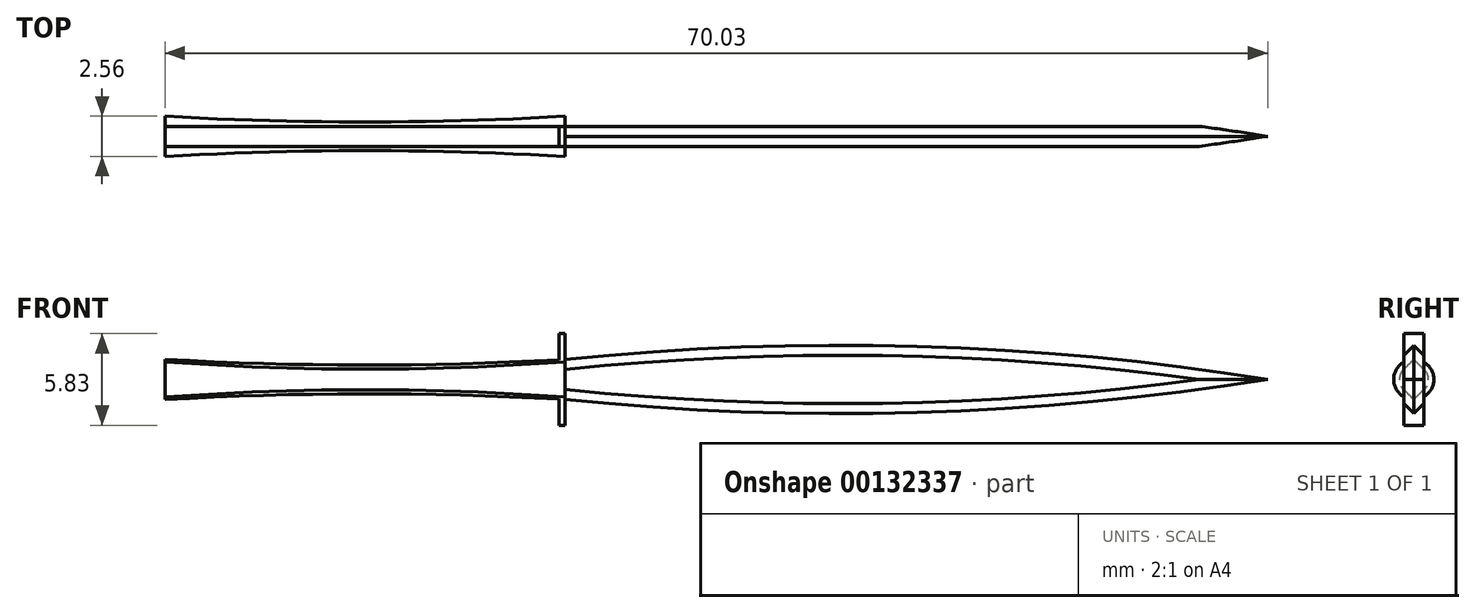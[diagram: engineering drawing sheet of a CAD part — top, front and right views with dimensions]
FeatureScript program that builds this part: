
annotation { "Feature Type Name" : "Feature", "Feature Type Description" : "" }
export const myFeature = defineFeature(function(context is Context, id is Id, definition is map)
    precondition{}
    {
        {
            var Q0;
            Q0=qCreatedBy(makeId("Front.planeOp"),FACE);
            var sketch = newSketch(context, id + "F0", { "sketchPlane" : qUnion([Q0])});
            skLineSegment(sketch, "E0", {"start": v(0, 0) * mm, "end": v(0, 2.55) * mm});
            skLineSegment(sketch, "E1", {"start": v(-25.4, 2.55) * mm, "end": v(-25.4, 0) * mm});
            skLineSegment(sketch, "E2", {"start": v(-25.4, 1.28) * mm, "end": v(0, 1.28) * mm});
            skLineSegment(sketch, "E3", {"start": v(0, 2.55) * mm, "end": v(0, 4.2) * mm});
            skLineSegment(sketch, "E4", {"start": v(0, 4.2) * mm, "end": v(-0.39, 4.2) * mm});
            skLineSegment(sketch, "E5.MirrorCS", {"start": v(0, -1.64) * mm, "end": v(-0.39, -1.64) * mm});
            skLineSegment(sketch, "E6.MirrorCS", {"start": v(0, 0) * mm, "end": v(0, -1.64) * mm});
            skLineSegment(sketch, "E7", {"start": v(0, 1.28) * mm, "end": v(44.62, 1.28) * mm});
            skArc(sketch, "E8", {"start": v(-25.4, 2.55) * mm, "mid": v(-12.7, 2.19) * mm, "end": v(0, 2.55) * mm});
            skArc(sketch, "E9.MirrorCS", {"start": v(-25.4, 0) * mm, "mid": v(-12.7, 0.36) * mm, "end": v(0, 0) * mm});
            skLineSegment(sketch, "E10", {"start": v(-0.39, 4.2) * mm, "end": v(-0.39, 2.53) * mm});
            skLineSegment(sketch, "E11", {"start": v(-0.39, -1.64) * mm, "end": v(-0.39, 0.02) * mm});
            skArc(sketch, "E12", {"start": v(44.62, 1.28) * mm, "mid": v(22.35, 3.37) * mm, "end": v(0, 2.55) * mm});
            skArc(sketch, "E13.MirrorCS", {"start": v(44.62, 1.28) * mm, "mid": v(22.35, -0.82) * mm, "end": v(0, 0) * mm});
            skSolve(sketch);
        }
        {
            var Q0;
            {var subQ4=sQuery(id+"F0.wireOp",EDGE,"E2");Q0=makeQuery(id+"F0.imprint","IMPRINT",FACE,{"disambiguationData":[TD([[makeQuery(id+"F0.imprint","IMPRINT",EDGE,{"derivedFrom":subQ4}),1.0]])]});}
            var Q1;
            Q1=sQuery(id+"F0.wireOp",EDGE,"E2");
            revolve(context, id + "F1", {"entities" : qUnion([Q0]), "axis" : qUnion([Q1]), "revolveType" : RevolveType.FULL});
        }
        {
            var Q0;
            Q0 = qSketchRegion(id + "F0", true);
            extrude(context, id + "F2", {"entities" : qUnion([Q0]), "operationType" : NewBodyOperationType.ADD, "endBound" : BoundingType.SYMMETRIC, "oppositeDirection" : true, "depth" : 1.27 * mm});
        }
        {
            var Q0;
            Q0=makeQuery(id+"F2.opExtrude","CAP_EDGE",EDGE,{"disambiguationData":[OSD([sQuery(id+"F0.wireOp",EDGE,"E12")])],"isStart":true});
            var Q1;
            Q1=makeQuery(id+"F2.opExtrude","CAP_EDGE",EDGE,{"disambiguationData":[OSD([sQuery(id+"F0.wireOp",EDGE,"E12")])],"isStart":false});
            var Q2;
            Q2=makeQuery(id+"F2.opExtrude","CAP_EDGE",EDGE,{"disambiguationData":[OSD([sQuery(id+"F0.wireOp",EDGE,"E13.MirrorCS")])],"isStart":false});
            var Q3;
            Q3=makeQuery(id+"F2.opExtrude","CAP_EDGE",EDGE,{"disambiguationData":[OSD([sQuery(id+"F0.wireOp",EDGE,"E13.MirrorCS")])],"isStart":true});
            chamfer(context, id + "F3", {"entities" : qUnion([Q0, Q1, Q2, Q3]), "width" : 0.64 * mm, "tangentPropagation" : true});
        }
    });
